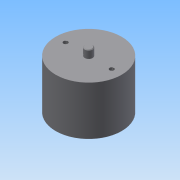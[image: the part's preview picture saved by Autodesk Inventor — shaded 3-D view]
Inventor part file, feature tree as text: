
AUTODESK INVENTOR PART (.ipt)
format: ipt  version: 2016 (Build 200138000, 138)  size: 112,640 bytes
history: native  units: mm
features: sketch x5, extrude x4, chamfer x1, hole x1, mirror x1, plane x1, projected_geometry x1
ambient origin geometry x8: Origin, YZ Plane, XZ Plane, XY Plane, X Axis, Y Axis, Z Axis, Center Point
bodies: Volumenkörper1 (feature_tree)
feature tree (14):
  extrude  "Extrusion1"  Depth=37.0mm TaperAngle=0.0deg
  extrude  "Extrusion2"  Depth=6.0mm TaperAngle=0.0deg
  extrude  "Extrusion3"  Depth=15.0mm TaperAngle=0.0deg
  chamfer  "Fase1"  Distance=0.5mm Angle=45.0deg
  hole  "Bohrung1"  [1 undecoded]
  mirror  "Spiegeln1"
  plane  "Arbeitsebene1"
  extrude  "Extrusion4"  Depth=5.0mm
  sketch  "Skizze1"  dims[d0=50.0mm d1=37.0mm d2=0.0mm]
  sketch  "Skizze2"  dims[d3=6.0mm d4=6.0mm d5=0.0mm]
  sketch  "Skizze3"  dims[d6=6.0mm d7=15.0mm d8=0.0mm d9=0.5mm d10=2.0mm d11=45.0deg]
  sketch  "Skizze4"  dims[d12=35.0mm]
  sketch  "Skizze5"  dims[d13=3.242mm d14=6.0mm d15=4.0mm d16=2.0mm d17=90.0deg d18=8.0mm d19=20.594885mm d20=15.0mm d21=5.0mm d22=2.0mm d23=2.0mm d24=0.0mm d25=0.0mm]
  projected_geometry  "Projizierte Kontur1"
note: 1 required parameter value undecoded (feature->parameter linkage not recoverable at this tier; creation-order binding heuristic only, values carry confidence <= 0.55)
